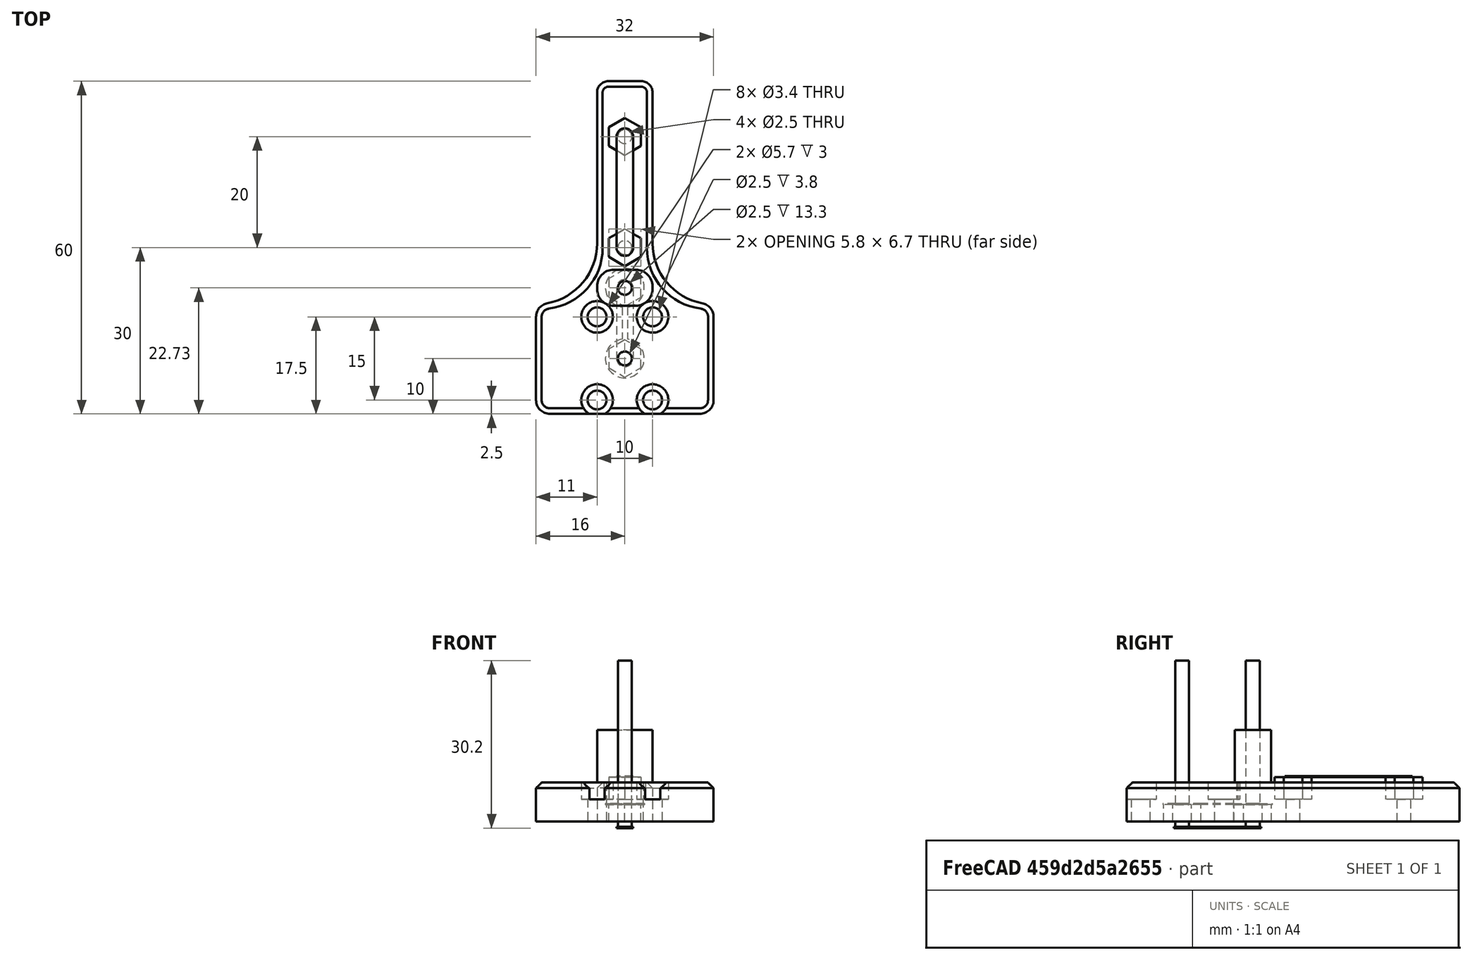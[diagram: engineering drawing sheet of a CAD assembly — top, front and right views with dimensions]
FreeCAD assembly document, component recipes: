
FREECAD ASSEMBLY — COMPONENT RECIPES ("miniXY-XYCarriage")

This assembly document has 4 components, labeled P0..P3 below (a component is one placed body or linked part). 4 of them carry a construction recipe — the FreeCAD feature program that regenerates the part from scratch, quoted from this document or its linked companion documents; the rest are supplied as boundary geometry only. No exploded tour is included for this assembly.
COMPONENT P0 — recipe-attached ("RailNutHoles", modeled in this document).
Construction recipe (the document's own serialized feature program — sketch geometry with constraints, then the solid features built on it; lengths are millimeters unless a unit is written):

FEATURE [Sketcher::SketchObject] Sketch009
  AttachmentOffset = pos=(0,0,8) rot=(0,0,1;0rad)
  FullyConstrained = true
  MapMode = 5
  Placement = pos=(0,0,8) rot=(0,0,1;0rad)
  Support = -> [XY_Plane013]
  expr: .AttachmentOffset.Base.z = <<Variables>>.CarriageThickness + 1
  sketch-geometry (4):
    g0: ArcOfCircle CenterX=0 CenterY=40 CenterZ=0 NormalX=0 NormalY=0 NormalZ=1 AngleXU=0 Radius=1.5 StartAngle=-1.91456e-11 EndAngle=3.14159
    g1: ArcOfCircle CenterX=0 CenterY=20 CenterZ=0 NormalX=0 NormalY=0 NormalZ=1 AngleXU=0 Radius=1.5 StartAngle=3.14159 EndAngle=6.28319
    g2: LineSegment StartX=-1.5 StartY=40 StartZ=0 EndX=-1.5 EndY=20 EndZ=0
    g3: LineSegment StartX=1.5 StartY=20 StartZ=0 EndX=1.5 EndY=40 EndZ=0
  constraints (10):
    c: PointOnObject(g0,g-2)
    c: PointOnObject(g1,g-2)
    c: Tangent(g2,g0) = -1.5708
    c: Tangent(g0,g3) = -1.5708
    c: Tangent(g2,g1) = -1.5708
    c: Tangent(g3,g1) = -1.5708
    c: Equal(g0,g1)
    c: Diameter(g0) = 3
    c: DistanceY(g1) = 20
    c: DistanceY(g1,g0) = 20
FEATURE [PartDesign::Pad] Pad006
  Direction = (0,0,1)
  Length = 0.2
  Length2 = 10
  Profile = -> Sketch009
  ReferenceAxis = -> Sketch009 [N_Axis]
  Type = 0
FEATURE [PartDesign::AdditivePrism] Prism003
  AttacherType = Attacher::AttachEngine3D
  AttachmentOffset = pos=(0,20,8) rot=(0.707107,0.707107,0;3.14159rad)
  BaseFeature = -> Pad006
  Circumradius = 3.35
  FirstAngle = 0
  Height = 4
  MapMode = 2
  Placement = pos=(0,20,8) rot=(0.707107,0.707107,0;3.14159rad)
  Polygon = 6
  SecondAngle = 0
  Support = -> [X_Axis013]
  expr: .AttachmentOffset.Base.z = <<Variables>>.CarriageThickness + 1
FEATURE [PartDesign::AdditivePrism] Prism004
  AttacherType = Attacher::AttachEngine3D
  AttachmentOffset = pos=(0,40,8) rot=(0.707107,0.707107,0;3.14159rad)
  BaseFeature = -> Prism003
  Circumradius = 3.35
  FirstAngle = 0
  Height = 4
  MapMode = 2
  Placement = pos=(0,40,8) rot=(0.707107,0.707107,0;3.14159rad)
  Polygon = 6
  SecondAngle = 0
  Support = -> [X_Axis013]
  expr: .AttachmentOffset.Base.z = <<Variables>>.CarriageThickness + 1
FEATURE [PartDesign::Body] Body008  label="RailNutHoles"
  Group = -> [Sketch009,Pad006,Prism003,Prism004]
  Origin = -> Origin013
  Tip = -> Prism004
COMPONENT P1 — recipe-attached ("CarriageBase", modeled in this document).
Construction recipe (the document's own serialized feature program — sketch geometry with constraints, then the solid features built on it; lengths are millimeters unless a unit is written):

FEATURE [PartDesign::Body] Body001  label="CarriageBaseBrace"
  Origin = -> Origin002
FEATURE [Sketcher::SketchObject] Sketch
  AttachmentOffset = pos=(0,0,6) rot=(0,0,1;0rad)
  FullyConstrained = true
  MapMode = 5
  Placement = pos=(0,0,6) rot=(0,0,1;0rad)
  Support = -> [XY_Plane001]
  expr: .AttachmentOffset.Base.z = <<Variables>>.CarriageThickness - 1
  sketch-geometry (18):
    g0: LineSegment StartX=-16 StartY=-7.5 StartZ=0 EndX=-16 EndY=7.5 EndZ=0
    g1: LineSegment StartX=16 StartY=7.5 StartZ=0 EndX=16 EndY=-7.5 EndZ=0
    g2: LineSegment StartX=13.5 StartY=-10 StartZ=0 EndX=-13.5 EndY=-10 EndZ=0
    g3: LineSegment StartX=-5 StartY=20.7665 StartZ=0 EndX=-5 EndY=48 EndZ=0
    g4: LineSegment StartX=-3 StartY=50 StartZ=0 EndX=3 EndY=50 EndZ=0
    g5: LineSegment StartX=5 StartY=48 StartZ=0 EndX=5 EndY=20.7665 EndZ=0
    g6: ArcOfCircle CenterX=-13.5 CenterY=-7.5 CenterZ=0 NormalX=0 NormalY=0 NormalZ=1 AngleXU=0 Radius=2.5 StartAngle=3.14159 EndAngle=4.71239
    g7: GeomPoint X=-16 Y=-10 Z=0
    g8: ArcOfCircle CenterX=13.5 CenterY=-7.5 CenterZ=0 NormalX=0 NormalY=0 NormalZ=1 AngleXU=0 Radius=2.5 StartAngle=4.71239 EndAngle=6.28319
    g9: GeomPoint X=16 Y=-10 Z=0
    g10: ArcOfCircle CenterX=13.5 CenterY=7.5 CenterZ=0 NormalX=0 NormalY=0 NormalZ=1 AngleXU=0 Radius=2.5 StartAngle=0 EndAngle=1.38454
    g11: ArcOfCircle CenterX=16 CenterY=20.7665 CenterZ=0 NormalX=0 NormalY=0 NormalZ=1 AngleXU=0 Radius=11 StartAngle=3.14159 EndAngle=4.52613
    g12: ArcOfCircle CenterX=-16 CenterY=20.7665 CenterZ=0 NormalX=0 NormalY=0 NormalZ=1 AngleXU=0 Radius=11 StartAngle=4.89865 EndAngle=6.28319
    g13: ArcOfCircle CenterX=-13.5 CenterY=7.5 CenterZ=0 NormalX=0 NormalY=0 NormalZ=1 AngleXU=0 Radius=2.5 StartAngle=1.75706 EndAngle=3.14159
    g14: ArcOfCircle CenterX=-3 CenterY=48 CenterZ=0 NormalX=0 NormalY=0 NormalZ=1 AngleXU=0 Radius=2 StartAngle=1.5708 EndAngle=3.14159
    g15: GeomPoint X=-5 Y=50 Z=0
    g16: ArcOfCircle CenterX=3 CenterY=48 CenterZ=0 NormalX=0 NormalY=0 NormalZ=1 AngleXU=0 Radius=2 StartAngle=-2.771e-13 EndAngle=1.5708
    g17: GeomPoint X=5 Y=50 Z=0
  constraints (39):
    c: PointOnObject(g7,g0)
    c: PointOnObject(g7,g2)
    c: Tangent(g0,g6) = 1.5708
    c: Tangent(g2,g6) = 1.5708
    c: PointOnObject(g9,g2)
    c: PointOnObject(g9,g1)
    c: Tangent(g2,g8) = 1.5708
    c: Tangent(g1,g8) = 1.5708
    c: Tangent(g1,g10) = 1.5708
    c: Tangent(g5,g11) = -1.5708
    c: Tangent(g3,g12) = -1.5708
    c: Tangent(g0,g13) = 1.5708
    c: PointOnObject(g15,g3)
    c: PointOnObject(g15,g4)
    c: Tangent(g3,g14) = 1.5708
    c: Tangent(g4,g14) = 1.5708
    c: PointOnObject(g17,g4)
    c: PointOnObject(g17,g5)
    c: Tangent(g4,g16) = 1.5708
    c: Tangent(g5,g16) = 1.5708
    c: Equal(g6,g13)
    c: Equal(g6,g8)
    c: Equal(g14,g16)
    c: Tangent(g13,g12) = 1.5708
    c: Tangent(g10,g11) = 1.5708
    c: PointOnObject(g12,g0)
    c: Radius(g14) = 2
    c: Radius(g6) = 2.5
    c: Symmetric(g14,g16,g-2)
    c: Symmetric(g6,g8,g-2)
    c: Symmetric(g13,g6,g-1)
    c: Symmetric(g13,g10,g-2)
    c: DistanceX(g14,g16) = 6
    c: DistanceY(g14) = 48
    c: Symmetric(g12,g11,g-2)
    c: DistanceY(g6,g13) = 15
    c: DistanceX(g6,g8) = 27
    c: Vertical(g3)
    c: Equal(g6,g10)
FEATURE [Sketcher::SketchObject] Sketch001
  AttachmentOffset = pos=(0,0,7) rot=(0,0,1;0rad)
  FullyConstrained = true
  MapMode = 5
  Placement = pos=(0,0,7) rot=(0,0,1;0rad)
  Support = -> [XY_Plane001]
  expr: .AttachmentOffset.Base.z = <<Variables>>.CarriageThickness
  expr: Constraints[26] = Sketch.Constraints[26] - 1mm
  expr: Constraints[27] = Sketch.Constraints[27] - 1mm
  expr: Constraints[32] = Sketch.Constraints[32]
  expr: Constraints[33] = Sketch.Constraints[33]
  expr: Constraints[35] = Sketch.Constraints[35]
  expr: Constraints[36] = Sketch.Constraints[36]
  sketch-geometry (18):
    g0: LineSegment StartX=-15 StartY=-7.5 StartZ=0 EndX=-15 EndY=7.5 EndZ=0
    g1: LineSegment StartX=15 StartY=7.5 StartZ=0 EndX=15 EndY=-7.5 EndZ=0
    g2: LineSegment StartX=13.5 StartY=-9 StartZ=0 EndX=-13.5 EndY=-9 EndZ=0
    g3: LineSegment StartX=-4 StartY=19.9097 StartZ=0 EndX=-4 EndY=48 EndZ=0
    g4: LineSegment StartX=-3 StartY=49 StartZ=0 EndX=3 EndY=49 EndZ=0
    g5: LineSegment StartX=4 StartY=48 StartZ=0 EndX=4 EndY=19.9097 EndZ=0
    g6: ArcOfCircle CenterX=-13.5 CenterY=-7.5 CenterZ=0 NormalX=0 NormalY=0 NormalZ=1 AngleXU=0 Radius=1.5 StartAngle=3.14159 EndAngle=4.71239
    g7: GeomPoint X=-15 Y=-9 Z=0
    g8: ArcOfCircle CenterX=13.5 CenterY=-7.5 CenterZ=0 NormalX=0 NormalY=0 NormalZ=1 AngleXU=0 Radius=1.5 StartAngle=4.71239 EndAngle=6.28319
    g9: GeomPoint X=15 Y=-9 Z=0
    g10: ArcOfCircle CenterX=13.5 CenterY=7.5 CenterZ=0 NormalX=0 NormalY=0 NormalZ=1 AngleXU=0 Radius=1.5 StartAngle=1e-16 EndAngle=1.45051
    g11: ArcOfCircle CenterX=15 CenterY=19.9097 CenterZ=0 NormalX=0 NormalY=0 NormalZ=1 AngleXU=0 Radius=11 StartAngle=3.14159 EndAngle=4.5921
    g12: ArcOfCircle CenterX=-15 CenterY=19.9097 CenterZ=0 NormalX=0 NormalY=0 NormalZ=1 AngleXU=0 Radius=11 StartAngle=4.83268 EndAngle=6.28319
    g13: ArcOfCircle CenterX=-13.5 CenterY=7.5 CenterZ=0 NormalX=0 NormalY=0 NormalZ=1 AngleXU=0 Radius=1.5 StartAngle=1.69109 EndAngle=3.14159
    g14: ArcOfCircle CenterX=-3 CenterY=48 CenterZ=0 NormalX=0 NormalY=0 NormalZ=1 AngleXU=0 Radius=1 StartAngle=1.5708 EndAngle=3.14159
    g15: GeomPoint X=-4 Y=49 Z=0
    g16: ArcOfCircle CenterX=3 CenterY=48 CenterZ=0 NormalX=0 NormalY=0 NormalZ=1 AngleXU=0 Radius=1 StartAngle=1e-16 EndAngle=1.5708
    g17: GeomPoint X=4 Y=49 Z=0
  constraints (39):
    c: PointOnObject(g7,g0)
    c: PointOnObject(g7,g2)
    c: Tangent(g0,g6) = 1.5708
    c: Tangent(g2,g6) = 1.5708
    c: PointOnObject(g9,g2)
    c: PointOnObject(g9,g1)
    c: Tangent(g2,g8) = 1.5708
    c: Tangent(g1,g8) = 1.5708
    c: Tangent(g1,g10) = 1.5708
    c: Tangent(g5,g11) = -1.5708
    c: Tangent(g3,g12) = -1.5708
    c: Tangent(g0,g13) = 1.5708
    c: PointOnObject(g15,g3)
    c: PointOnObject(g15,g4)
    c: Tangent(g3,g14) = 1.5708
    c: Tangent(g4,g14) = 1.5708
    c: PointOnObject(g17,g4)
    c: PointOnObject(g17,g5)
    c: Tangent(g4,g16) = 1.5708
    c: Tangent(g5,g16) = 1.5708
    c: Equal(g6,g13)
    c: Equal(g6,g8)
    c: Equal(g14,g16)
    c: Tangent(g13,g12) = 1.5708
    c: Tangent(g10,g11) = 1.5708
    c: PointOnObject(g12,g0)
    c: Radius(g14) = 1
    c: Radius(g6) = 1.5
    c: Symmetric(g14,g16,g-2)
    c: Symmetric(g6,g8,g-2)
    c: Symmetric(g13,g6,g-1)
    c: Symmetric(g13,g10,g-2)
    c: DistanceX(g14,g16) = 6
    c: DistanceY(g14) = 48
    c: Symmetric(g12,g11,g-2)
    c: DistanceY(g6,g13) = 15
    c: DistanceX(g6,g8) = 27
    c: Vertical(g3)
    c: Equal(g6,g10)
FEATURE [PartDesign::Pad] Pad
  Direction = (0,0,1)
  Length = 6
  Length2 = 10
  Profile = -> Sketch
  ReferenceAxis = -> Sketch [N_Axis]
  Reversed = true
  Type = 0
  expr: Length = <<Variables>>.CarriageThickness - 1
FEATURE [PartDesign::AdditiveLoft] AdditiveLoft
  BaseFeature = -> Pad
  Closed = false
  Profile = -> Sketch
  Ruled = false
  Sections = -> [Sketch001]
FEATURE [Sketcher::SketchObject] Sketch002
  AttachmentOffset = pos=(0,0,7) rot=(0,0,1;0rad)
  FullyConstrained = true
  MapMode = 5
  Placement = pos=(0,0,7) rot=(0,0,1;0rad)
  Support = -> [XY_Plane001]
  expr: .AttachmentOffset.Base.z = <<Variables>>.CarriageThickness
  sketch-geometry (4):
    g0: Circle CenterX=-5 CenterY=7.5 CenterZ=0 NormalX=0 NormalY=0 NormalZ=1 AngleXU=0 Radius=1.5
    g1: Circle CenterX=5 CenterY=7.5 CenterZ=0 NormalX=0 NormalY=0 NormalZ=1 AngleXU=0 Radius=1.5
    g2: Circle CenterX=-5 CenterY=-7.5 CenterZ=0 NormalX=0 NormalY=0 NormalZ=1 AngleXU=0 Radius=1.5
    g3: Circle CenterX=5 CenterY=-7.5 CenterZ=0 NormalX=0 NormalY=0 NormalZ=1 AngleXU=0 Radius=1.5
  constraints (9):
    c: Symmetric(g0,g1,g-2)
    c: Symmetric(g0,g2,g-1)
    c: Symmetric(g1,g3,g-1)
    c: Equal(g0,g1)
    c: Equal(g0,g2)
    c: Equal(g0,g3)
    c: Diameter(g0) = 3
    c: DistanceX(g0,g1) = 10
    c: DistanceY(g2,g0) = 15
FEATURE [Sketcher::SketchObject] Sketch003  label="SketchIdlerHole"
  AttachmentOffset = pos=(0,0,-1) rot=(0,0,1;0rad)
  FullyConstrained = true
  MapMode = 5
  Placement = pos=(0,0,-1) rot=(0,0,1;0rad)
  Support = -> [XY_Plane011]
  expr: Constraints[2] = <<Variables>>.IdlerDiameter
  sketch-geometry (2):
    g0: Circle CenterX=0 CenterY=0 CenterZ=0 NormalX=0 NormalY=0 NormalZ=1 AngleXU=0 Radius=1.25
    g1: Circle CenterX=0 CenterY=12.73 CenterZ=0 NormalX=0 NormalY=0 NormalZ=1 AngleXU=0 Radius=1.25
  constraints (5):
    c: Coincident(g0,g-1)
    c: PointOnObject(g1,g-2)
    c: DistanceY(g1) = 12.73
    c: Equal(g1,g0)
    c: Diameter(g1) = 2.5
FEATURE [PartDesign::Hole] Hole
  BaseFeature = -> AdditiveLoft
  CustomThreadClearance = 0
  Depth = 25
  DepthType = 0
  Diameter = 3.4
  DrillForDepth = false
  DrillPoint = 1
  DrillPointAngle = 118
  HoleCutCountersinkAngle = 90
  HoleCutCustomValues = false
  HoleCutDepth = 3
  HoleCutDiameter = 5.7
  HoleCutType = 1
  ModelThread = false
  Profile = -> Sketch002
  Tapered = false
  TaperedAngle = 90
  ThreadClass = 0
  ThreadDepth = 25
  ThreadDepthType = 0
  ThreadDirection = 0
  ThreadFit = 0
  ThreadSize = 9
  ThreadType = 1
  Threaded = false
  UseCustomThreadClearance = false
FEATURE [Sketcher::SketchObject] Sketch004
  FullyConstrained = true
  MapMode = 5
  Support = -> [XY_Plane001]
  sketch-geometry (2):
    g0: Circle CenterX=0 CenterY=20 CenterZ=0 NormalX=0 NormalY=0 NormalZ=1 AngleXU=0 Radius=1.5
    g1: Circle CenterX=0 CenterY=40 CenterZ=0 NormalX=0 NormalY=0 NormalZ=1 AngleXU=0 Radius=1.5
  constraints (6):
    c: PointOnObject(g1,g-2)
    c: PointOnObject(g0,g-2)
    c: Equal(g1,g0)
    c: Diameter(g1) = 3
    c: DistanceY(g0) = 20
    c: DistanceY(g0,g1) = 20
FEATURE [PartDesign::Hole] Hole001
  BaseFeature = -> Hole
  CustomThreadClearance = 0
  Depth = 25
  DepthType = 0
  Diameter = 2.5
  DrillForDepth = false
  DrillPoint = 1
  DrillPointAngle = 118
  HoleCutCountersinkAngle = 90
  HoleCutCustomValues = false
  HoleCutDepth = 0
  HoleCutDiameter = 6.1
  HoleCutType = 0
  ModelThread = false
  Profile = -> Sketch004
  Reversed = true
  Tapered = false
  TaperedAngle = 90
  ThreadClass = 0
  ThreadDepth = 25
  ThreadDepthType = 0
  ThreadDirection = 0
  ThreadFit = 0
  ThreadSize = 9
  ThreadType = 1
  Threaded = true
  UseCustomThreadClearance = false
FEATURE [Sketcher::SketchObject] Sketch007
  AttachmentOffset = pos=(0,0,3) rot=(0,0,1;0rad)
  FullyConstrained = true
  MapMode = 5
  Placement = pos=(0,0,3) rot=(0,0,1;0rad)
  Support = -> [XY_Plane012]
  expr: Constraints[9] = <<Variables>>.IdlerDiameter
  sketch-geometry (4):
    g0: ArcOfCircle CenterX=0 CenterY=0 CenterZ=0 NormalX=0 NormalY=0 NormalZ=1 AngleXU=0 Radius=3.5 StartAngle=1.71414 EndAngle=7.71063
    g1: ArcOfCircle CenterX=-2.1e-15 CenterY=12.73 CenterZ=0 NormalX=0 NormalY=0 NormalZ=1 AngleXU=0 Radius=3.5 StartAngle=4.85574 EndAngle=10.8522
    g2: LineSegment StartX=-0.5 StartY=9.2659 StartZ=0 EndX=-0.5 EndY=3.4641 EndZ=0
    g3: LineSegment StartX=0.5 StartY=9.2659 StartZ=0 EndX=0.5 EndY=3.4641 EndZ=0
  constraints (12):
    c: Coincident(g2,g1)
    c: Coincident(g2,g0)
    c: Coincident(g3,g1)
    c: Coincident(g3,g0)
    c: Coincident(g0,g-1)
    c: Symmetric(g1,g1,g-2)
    c: Symmetric(g0,g0,g-2)
    c: Equal(g1,g0)
    c: Diameter(g1) = 7
    c: DistanceY(g1) = 12.73
    c: DistanceX(g1,g1) = 1
    c: Vertical(g2)
FEATURE [PartDesign::Pad] Pad003
  Direction = (0,0,1)
  Length = 0.2
  Length2 = 10
  Profile = -> Sketch007
  ReferenceAxis = -> Sketch007 [N_Axis]
  Type = 0
FEATURE [PartDesign::Body] Body007  label="IdlerNutHoleSupport"
  Group = -> [Pad003,Sketch007]
  Origin = -> Origin012
  Tip = -> Pad003
FEATURE [Sketcher::SketchObject] Sketch008
  AttachmentOffset = pos=(0,0,-1) rot=(0,0,1;0rad)
  FullyConstrained = true
  MapMode = 5
  Placement = pos=(0,0,-1) rot=(0,0,1;0rad)
  Support = -> [XY_Plane011]
  expr: Constraints[8] = <<Variables>>.IdlerDiameter
  sketch-geometry (4):
    g0: ArcOfCircle CenterX=0 CenterY=0 CenterZ=0 NormalX=0 NormalY=0 NormalZ=1 AngleXU=0 Radius=1.5 StartAngle=3.14159 EndAngle=6.28319
    g1: ArcOfCircle CenterX=0 CenterY=12.73 CenterZ=0 NormalX=0 NormalY=0 NormalZ=1 AngleXU=0 Radius=1.5 StartAngle=2e-16 EndAngle=3.14159
    g2: LineSegment StartX=-1.5 StartY=12.73 StartZ=0 EndX=-1.5 EndY=0 EndZ=0
    g3: LineSegment StartX=1.5 StartY=12.73 StartZ=0 EndX=1.5 EndY=0 EndZ=0
  constraints (9):
    c: Coincident(g0,g-1)
    c: PointOnObject(g1,g-2)
    c: Tangent(g1,g2) = -1.5708
    c: Tangent(g1,g3) = 1.5708
    c: Tangent(g2,g0) = -1.5708
    c: Tangent(g3,g0) = 1.5708
    c: Equal(g0,g1)
    c: Diameter(g0) = 3
    c: DistanceY(g1) = 12.73
FEATURE [PartDesign::Pad] Pad004
  Direction = (0,0,1)
  Length = 0.2
  Length2 = 10
  Profile = -> Sketch008
  ReferenceAxis = -> Sketch008 [N_Axis]
  Reversed = true
  Type = 0
FEATURE [PartDesign::Pad] Pad005
  BaseFeature = -> Pad004
  Direction = (0,0,1)
  Length = 30
  Length2 = 10
  Profile = -> Sketch003
  ReferenceAxis = -> Sketch003 [N_Axis]
  Type = 0
FEATURE [PartDesign::AdditivePrism] Prism
  AttacherType = Attacher::AttachEngine3D
  AttachmentOffset = pos=(0,0,0) rot=(0,0,1;1.5708rad)
  BaseFeature = -> Pad005
  Circumradius = 3.35
  FirstAngle = 0
  Height = 3
  MapMode = 2
  Placement = pos=(0,0,0) rot=(0,0,1;1.5708rad)
  Polygon = 6
  SecondAngle = 0
  Support = -> [X_Axis011]
FEATURE [PartDesign::AdditivePrism] Prism001
  AttacherType = Attacher::AttachEngine3D
  AttachmentOffset = pos=(0,12.73,0) rot=(0,0,1;1.5708rad)
  BaseFeature = -> Prism
  Circumradius = 3.35
  FirstAngle = 0
  Height = 3
  MapMode = 2
  Placement = pos=(0,12.73,0) rot=(0,0,1;1.5708rad)
  Polygon = 6
  SecondAngle = 0
  Support = -> [X_Axis011]
  expr: .AttachmentOffset.Base.y = <<Variables>>.IdlerDiameter
FEATURE [PartDesign::Body] Body006  label="IdlerNutHoles"
  Group = -> [Pad004,Pad005,Prism,Sketch003,Sketch008,Prism001]
  Origin = -> Origin011
  Tip = -> Prism001
FEATURE [PartDesign::Boolean] Boolean
  BaseFeature = -> Hole001
  Group = -> [Body008]
  Type = 1
FEATURE [PartDesign::Body] Body  label="CarriageBaseMain"
  Group = -> [Sketch,Sketch001,Pad,AdditiveLoft,Sketch002,Hole,Sketch004,Hole001,Boolean]
  Origin = -> Origin001
  Tip = -> Boolean
COMPONENT P2 — recipe-attached ("CarriageLeft", modeled in this document).
Construction recipe (the document's own serialized feature program — sketch geometry with constraints, then the solid features built on it; lengths are millimeters unless a unit is written):

FEATURE [PartDesign::Body] Body003  label="CarriageLeftBrace"
  Origin = -> Origin005
FEATURE [Sketcher::SketchObject] Sketch005
  FullyConstrained = true
  MapMode = 5
  Support = -> [XY_Plane004]
  sketch-geometry (12):
    g0: LineSegment StartX=-2 StartY=16 StartZ=0 EndX=2 EndY=16 EndZ=0
    g1: LineSegment StartX=5 StartY=13 StartZ=0 EndX=5 EndY=12.5 EndZ=0
    g2: LineSegment StartX=2 StartY=9.5 StartZ=0 EndX=-2 EndY=9.5 EndZ=0
    g3: LineSegment StartX=-5 StartY=12.5 StartZ=0 EndX=-5 EndY=13 EndZ=0
    g4: ArcOfCircle CenterX=-2 CenterY=13 CenterZ=0 NormalX=0 NormalY=0 NormalZ=1 AngleXU=0 Radius=3 StartAngle=1.5708 EndAngle=3.14159
    g5: GeomPoint X=-5 Y=16 Z=0
    g6: ArcOfCircle CenterX=2 CenterY=13 CenterZ=0 NormalX=0 NormalY=0 NormalZ=1 AngleXU=0 Radius=3 StartAngle=0 EndAngle=1.5708
    g7: GeomPoint X=5 Y=16 Z=0
    g8: ArcOfCircle CenterX=-2 CenterY=12.5 CenterZ=0 NormalX=0 NormalY=0 NormalZ=1 AngleXU=0 Radius=3 StartAngle=3.14159 EndAngle=4.71239
    g9: GeomPoint X=-5 Y=9.5 Z=0
    g10: ArcOfCircle CenterX=2 CenterY=12.5 CenterZ=0 NormalX=0 NormalY=0 NormalZ=1 AngleXU=0 Radius=3 StartAngle=4.71239 EndAngle=6.28319
    g11: GeomPoint X=5 Y=9.5 Z=0
  constraints (27):
    c: Horizontal(g0)
    c: Vertical(g1)
    c: Vertical(g3)
    c: PointOnObject(g5,g0)
    c: PointOnObject(g5,g3)
    c: Tangent(g0,g4) = 1.5708
    c: Tangent(g3,g4) = 1.5708
    c: PointOnObject(g7,g0)
    c: PointOnObject(g7,g1)
    c: Tangent(g0,g6) = 1.5708
    c: Tangent(g1,g6) = 1.5708
    c: PointOnObject(g9,g2)
    c: PointOnObject(g9,g3)
    c: Tangent(g2,g8) = 1.5708
    c: Tangent(g3,g8) = 1.5708
    c: PointOnObject(g11,g2)
    c: PointOnObject(g11,g1)
    c: Tangent(g2,g10) = 1.5708
    c: Tangent(g1,g10) = 1.5708
    c: Equal(g4,g6)
    c: Equal(g4,g10)
    c: Equal(g4,g8)
    c: Radius(g4) = 3
    c: DistanceY(g9,g5) = 6.5
    c: Symmetric(g9,g11,g-2)
    c: DistanceX(g9,g11) = 10
    c: DistanceY(g9) = 9.5
FEATURE [PartDesign::Pad] Pad001
  Direction = (0,0,1)
  Length = 16.5
  Length2 = 10
  Profile = -> Sketch005
  ReferenceAxis = -> Sketch005 [N_Axis]
  Type = 0
  expr: Length = <<Variables>>.CarriageThickness + <<Variables>>.WasherThickness * 2 + <<Variables>>.IdlerHeight
FEATURE [PartDesign::Boolean] Boolean001
  BaseFeature = -> Pad001
  Group = -> [Clone004]
  Type = 0
FEATURE [PartDesign::Boolean] Boolean003
  BaseFeature = -> Boolean001
  Group = -> [ShapeBinder001]
  Type = 1
FEATURE [PartDesign::Boolean] Boolean004
  BaseFeature = -> Boolean003
  Group = -> [ShapeBinder]
  Refine = true
  Type = 0
FEATURE [PartDesign::Body] Body002  label="CarriageLeftMain"
  Group = -> [Sketch005,Pad001,Boolean001,Boolean003,Boolean004]
  Origin = -> Origin004
  Tip = -> Boolean004
COMPONENT P3 — recipe-attached ("CarriageRight", modeled in this document).
Construction recipe (the document's own serialized feature program — sketch geometry with constraints, then the solid features built on it; lengths are millimeters unless a unit is written):

FEATURE [PartDesign::Body] Body005  label="CarriageRightBrace"
  Origin = -> Origin009
FEATURE [Sketcher::SketchObject] Sketch006
  FullyConstrained = true
  MapMode = 5
  Support = -> [XY_Plane008]
  sketch-geometry (12):
    g0: LineSegment StartX=-2 StartY=3.25 StartZ=0 EndX=2 EndY=3.25 EndZ=0
    g1: LineSegment StartX=5 StartY=0.25 StartZ=0 EndX=5 EndY=-0.25 EndZ=0
    g2: LineSegment StartX=2 StartY=-3.25 StartZ=0 EndX=-2 EndY=-3.25 EndZ=0
    g3: LineSegment StartX=-5 StartY=-0.25 StartZ=0 EndX=-5 EndY=0.25 EndZ=0
    g4: ArcOfCircle CenterX=-2 CenterY=0.25 CenterZ=0 NormalX=0 NormalY=0 NormalZ=1 AngleXU=0 Radius=3 StartAngle=1.5708 EndAngle=3.14159
    g5: GeomPoint X=-5 Y=3.25 Z=0
    g6: ArcOfCircle CenterX=2 CenterY=0.25 CenterZ=0 NormalX=0 NormalY=0 NormalZ=1 AngleXU=0 Radius=3 StartAngle=0 EndAngle=1.5708
    g7: GeomPoint X=5 Y=3.25 Z=0
    g8: ArcOfCircle CenterX=-2 CenterY=-0.25 CenterZ=0 NormalX=0 NormalY=0 NormalZ=1 AngleXU=0 Radius=3 StartAngle=3.14159 EndAngle=4.71239
    g9: GeomPoint X=-5 Y=-3.25 Z=0
    g10: ArcOfCircle CenterX=2 CenterY=-0.25 CenterZ=0 NormalX=0 NormalY=0 NormalZ=1 AngleXU=0 Radius=3 StartAngle=4.71239 EndAngle=6.28319
    g11: GeomPoint X=5 Y=-3.25 Z=0
  constraints (27):
    c: Horizontal(g0)
    c: Horizontal(g2)
    c: Vertical(g1)
    c: Vertical(g3)
    c: PointOnObject(g5,g0)
    c: PointOnObject(g5,g3)
    c: Tangent(g0,g4) = 1.5708
    c: Tangent(g3,g4) = 1.5708
    c: PointOnObject(g7,g0)
    c: PointOnObject(g7,g1)
    c: Tangent(g0,g6) = 1.5708
    c: Tangent(g1,g6) = 1.5708
    c: PointOnObject(g9,g2)
    c: PointOnObject(g9,g3)
    c: Tangent(g2,g8) = 1.5708
    c: Tangent(g3,g8) = 1.5708
    c: PointOnObject(g11,g2)
    c: PointOnObject(g11,g1)
    c: Tangent(g2,g10) = 1.5708
    c: Tangent(g1,g10) = 1.5708
    c: Equal(g4,g6)
    c: Equal(g4,g10)
    c: Equal(g4,g8)
    c: Radius(g4) = 3
    c: Symmetric(g5,g11,g-1)
    c: DistanceY(g9,g5) = 6.5
    c: DistanceX(g5,g7) = 10
FEATURE [PartDesign::Pad] Pad002
  Direction = (0,0,1)
  Length = 16.5
  Length2 = 10
  Profile = -> Sketch006
  ReferenceAxis = -> Sketch006 [N_Axis]
  Type = 0
  expr: Length = <<Variables>>.CarriageThickness + <<Variables>>.WasherThickness * 2 + <<Variables>>.IdlerHeight
FEATURE [PartDesign::Boolean] Boolean002
  BaseFeature = -> Pad002
  Group = -> [Clone005]
  Type = 0
FEATURE [PartDesign::Boolean] Boolean005
  BaseFeature = -> Boolean002
  Group = -> [ShapeBinder003]
  Type = 1
FEATURE [PartDesign::Boolean] Boolean006
  BaseFeature = -> Boolean005
  Group = -> [ShapeBinder002]
  Refine = true
  Type = 0
FEATURE [PartDesign::Body] Body004  label="CarriageRightMain"
  Group = -> [Sketch006,Pad002,Boolean002,Boolean005,Boolean006]
  Origin = -> Origin008
  Tip = -> Boolean006
PROVENANCE & LICENSES
A FreeCAD (.FCStd) document from a public repository crawl; recipes are the document's own serialized feature recipes (and, for linked parts, companion documents' recipes).
License: gpl-3.0.
